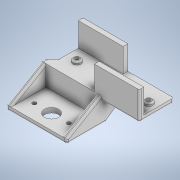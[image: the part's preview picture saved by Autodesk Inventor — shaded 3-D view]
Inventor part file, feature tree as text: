
AUTODESK INVENTOR PART (.ipt)
format: ipt  version: 2022 (Build 260153000, 153)  size: 327,168 bytes
history: native  units: in
note: dims shown in document units (in); Inventor stores cm internally (conversion verified against a paired STEP export)
features: extrude x9, sketch x9, chamfer x2, fillet x1
ambient origin geometry x8: Origin, YZ Plane, XZ Plane, XY Plane, X Axis, Y Axis, Z Axis, Center Point
bodies: Solid1 (feature_tree)
feature tree (21):
  extrude  "Extrusion1"  Depth=1.4331in
  extrude  "Extrusion2"  Depth=0.1969in
  extrude  "Extrusion3"  Depth=0.1969in
  extrude  "Extrusion4"  Depth=0.1969in TaperAngle=0.0deg
  extrude  "Extrusion5"  Depth=0.3406in
  chamfer  "Chamfer1"  Distance=0.1181in
  extrude  "Extrusion6"  Depth=0.1575in
  extrude  "Extrusion7"  Depth=0.0787in
  extrude  "Extrusion8"  Depth=0.0787in TaperAngle=0.0deg
  chamfer  "Chamfer2"  Distance=0.2362in
  extrude  "Extrusion9"  Depth=0.0787in
  fillet  "Fillet2"  Radius=0.2362in
  sketch  "Sketch1"  dims[d0=3.7795in d1=1.4331in]
  sketch  "Sketch2"  dims[d2=0.1969in d3=0.0in d4=1.8701in]
  sketch  "Sketch3"  dims[d5=0.1969in d6=1.8701in]
  sketch  "Sketch4"  dims[d7=0.1969in d8=1.0in d9=0.0in]
  sketch  "Sketch5"  dims[d10=0.3406in d11=0.3406in]
  sketch  "Sketch6"  dims[d12=0.3406in]
  sketch  "Sketch7"  dims[d13=0.3406in d14=0.1181in d15=0.0in]
  sketch  "Sketch8"  dims[d16=0.1575in d17=0.1575in]
  sketch  "Sketch9"  dims[d18=0.1575in d19=0.1575in d20=0.4724in d21=0.0in d22=0.2362in d23=0.2362in d24=0.2362in d25=0.2362in d26=0.0984in d27=0.0in d28=0.0591in d29=0.0787in d30=45.0deg d33=2.5197in d34=0.1969in d35=0.1969in d36=0.1969in d37=0.1969in d38=0.8504in d39=0.0in d40=0.1969in d41=0.0in d42=0.1969in d43=0.1969in d44=0.1969in d45=1.4508in d46=0.0in d47=3.937in d48=0.0in d49=0.315in d50=0.0787in d51=45.0deg d52=0.5906in d53=0.1575in d54=0.1575in d55=0.2362in d56=0.0in d57=0.0787in]
